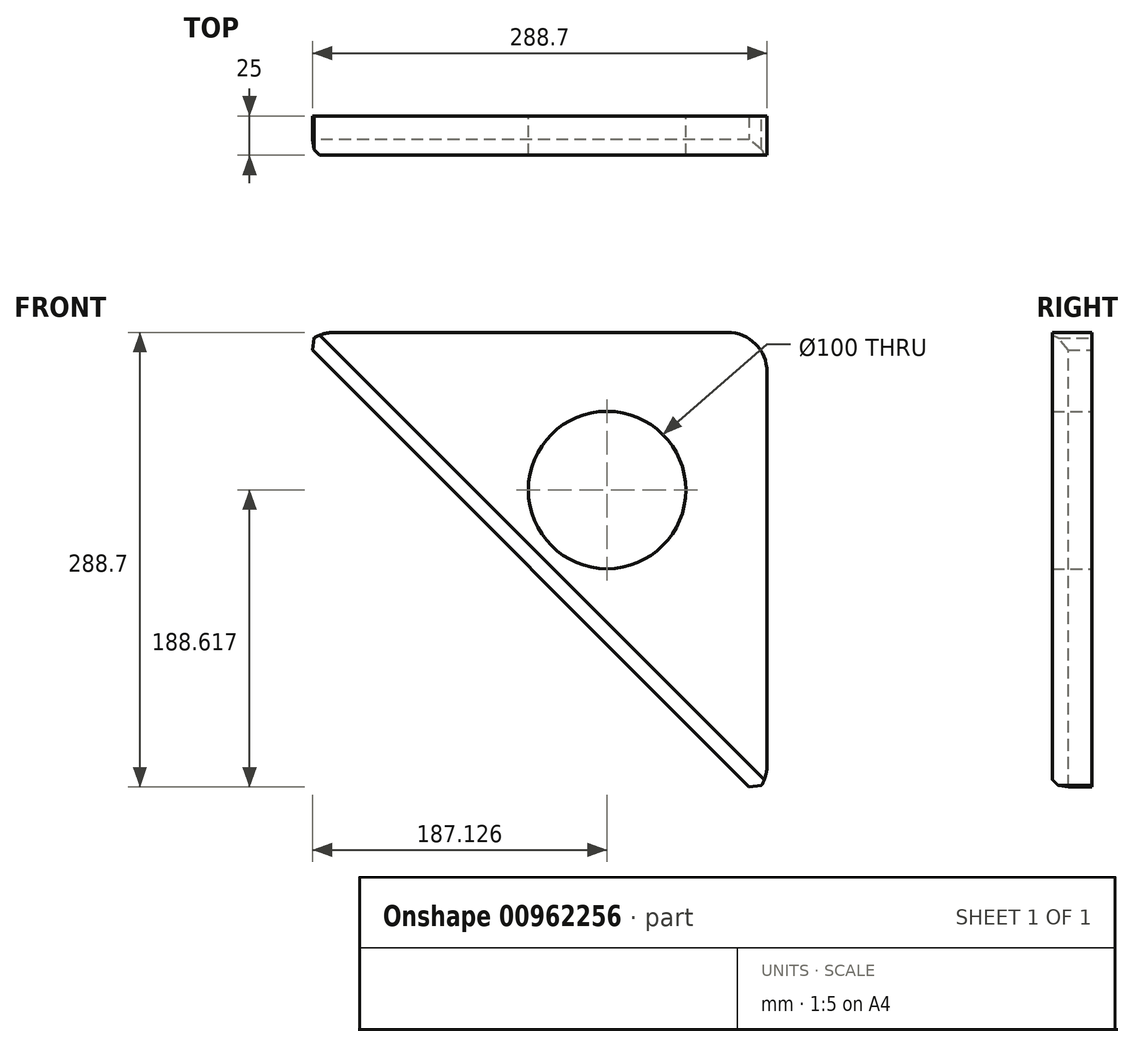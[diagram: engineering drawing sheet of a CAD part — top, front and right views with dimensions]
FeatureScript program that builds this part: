
annotation { "Feature Type Name" : "Feature", "Feature Type Description" : "" }
export const myFeature = defineFeature(function(context is Context, id is Id, definition is map)
    precondition{}
    {
        {
            var Q0;
            Q0=qCreatedBy(makeId("Front.planeOp"),FACE);
            var sketch = newSketch(context, id + "F0", { "sketchPlane" : qUnion([Q0])});
            skLineSegment(sketch, "E0.top", {"start": v(-198.92, 143.03) * mm, "end": v(51.08, 143.03) * mm});
            skLineSegment(sketch, "E0.right", {"start": v(76.08, -131.97) * mm, "end": v(76.08, 118.03) * mm});
            skCircle(sketch, "E1", {"center": v(-25.5, 42.95) * mm, "radius": 50 * mm});
            skArc(sketch, "E2.filletArc", {"start": v(76.08, 118.03) * mm, "mid": v(68.76, 135.7) * mm, "end": v(51.08, 143.03) * mm});
            skArc(sketch, "E3.filletArc", {"start": v(-198.92, 143.03) * mm, "mid": v(-208.49, 141.12) * mm, "end": v(-216.6, 135.7) * mm});
            skArc(sketch, "E4.filletArc", {"start": v(68.76, -149.65) * mm, "mid": v(74.17, -141.54) * mm, "end": v(76.08, -131.97) * mm});
            skLineSegment(sketch, "E5", {"start": v(-216.6, 135.7) * mm, "end": v(68.76, -149.65) * mm});
            skSolve(sketch);
        }
        {
            var Q0;
            Q0 = qSketchRegion(id + "F0", true);
            extrude(context, id + "F1", {"entities" : qUnion([Q0]), "depth" : 25 * mm, "offsetDistance" : 25 * mm});
        }
        {
            var Q0;
            Q0=makeQuery(id+"F1.opExtrude","CAP_EDGE",EDGE,{"disambiguationData":[OSD([sQuery(id+"F0.wireOp",EDGE,"E5")])],"isStart":false});
            chamfer(context, id + "F2", {"entities" : qUnion([Q0]), "width" : 10 * mm, "tangentPropagation" : true});
        }
        {
            var Q0;
            Q0=makeQuery(id+"F1.opExtrude","SWEPT_EDGE",EDGE,{"disambiguationData":[OSD([sQuery(id+"F0.wireOp",EDGE,"E4.filletArc"),sQuery(id+"F0.wireOp",EDGE,"E5")])]});
            var Q1;
            Q1=makeQuery(id+"F1.opExtrude","SWEPT_EDGE",EDGE,{"disambiguationData":[OSD([sQuery(id+"F0.wireOp",EDGE,"E3.filletArc"),sQuery(id+"F0.wireOp",EDGE,"E5")])]});
            chamfer(context, id + "F3", {"entities" : qUnion([Q0, Q1]), "width" : 5 * mm, "tangentPropagation" : true});
        }
    });
